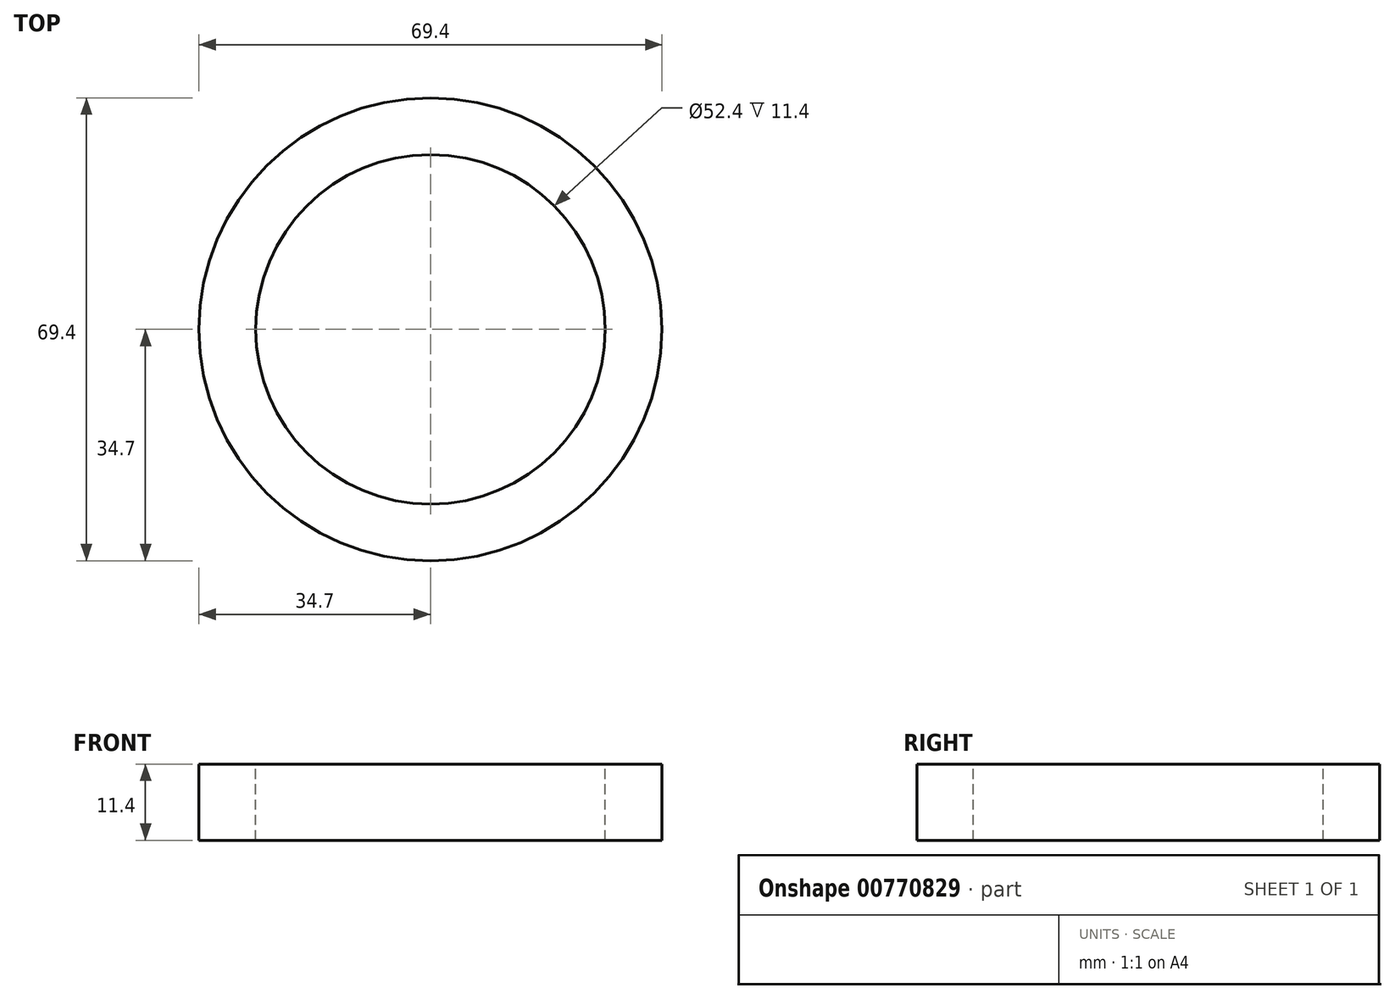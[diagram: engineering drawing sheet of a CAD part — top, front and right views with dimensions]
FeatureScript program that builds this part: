
annotation { "Feature Type Name" : "Feature", "Feature Type Description" : "" }
export const myFeature = defineFeature(function(context is Context, id is Id, definition is map)
    precondition{}
    {
        {
            var Q0;
            Q0=qCreatedBy(makeId("Front.planeOp"),FACE);
            var sketch = newSketch(context, id + "F0", { "sketchPlane" : qUnion([Q0])});
            skLineSegment(sketch, "E0", {"start": v(0, 172.54) * mm, "end": v(0, 0) * mm, "construction": true});
            skLineSegment(sketch, "E1", {"start": v(0, 0) * mm, "end": v(168.47, 0) * mm, "construction": true});
            skLineSegment(sketch, "E2.top", {"start": v(-26.2, 11.4) * mm, "end": v(-34.7, 11.4) * mm});
            skLineSegment(sketch, "E2.left", {"start": v(-26.2, 0) * mm, "end": v(-26.2, 11.4) * mm});
            skPoint(sketch, "E3.orphan", {"position": v(-34.7, 0) * mm});
            skLineSegment(sketch, "E4", {"start": v(-34.7, 11.4) * mm, "end": v(-34.7, 0) * mm});
            skLineSegment(sketch, "E5", {"start": v(-34.7, 0) * mm, "end": v(-26.2, 0) * mm});
            skSolve(sketch);
        }
        {
            var Q0;
            Q0=makeQuery(id+"F0.imprint","IMPRINT",FACE,{"disambiguationData":[TD([[makeQuery(id+"F0.imprint","IMPRINT",EDGE,{"derivedFrom":sQuery(id+"F0.wireOp",EDGE,"E2.top")}),1.0]])]});
            var Q1;
            Q1=sQuery(id+"F0.wireOp",EDGE,"E0");
            revolve(context, id + "F1", {"surfaceOperationType" : NewSurfaceOperationType.NEW, "entities" : qUnion([Q0]), "axis" : qUnion([Q1]), "revolveType" : RevolveType.FULL});
        }
    });
